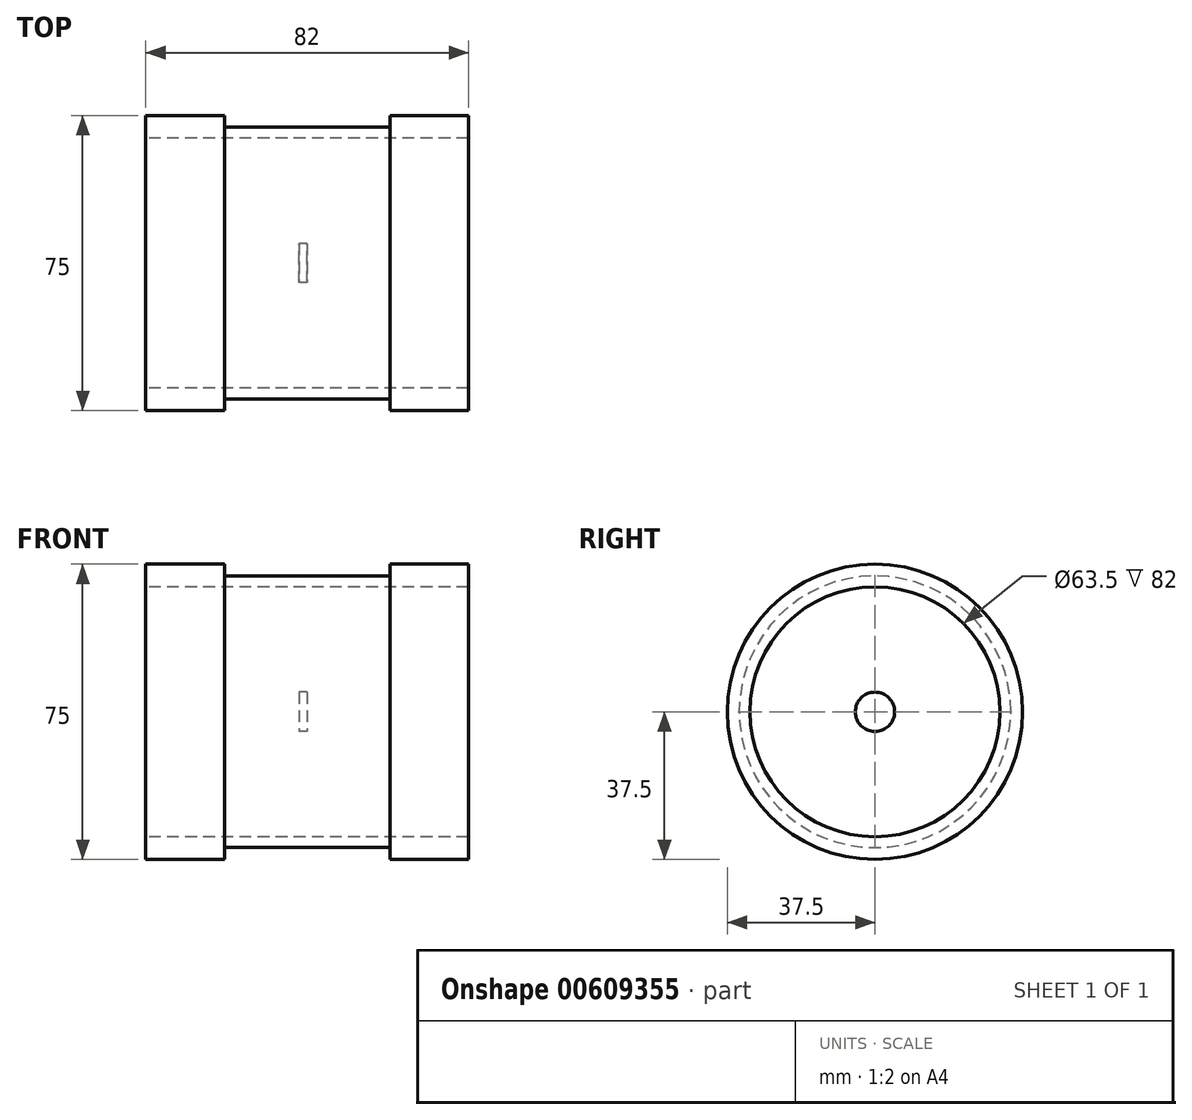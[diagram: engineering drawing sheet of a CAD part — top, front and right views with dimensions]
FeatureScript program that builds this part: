
annotation { "Feature Type Name" : "Feature", "Feature Type Description" : "" }
export const myFeature = defineFeature(function(context is Context, id is Id, definition is map)
    precondition{}
    {
        {
            var Q0;
            Q0=qCreatedBy(makeId("Front.planeOp"),FACE);
            var sketch = newSketch(context, id + "F0", { "sketchPlane" : qUnion([Q0])});
            skLineSegment(sketch, "E0", {"start": v(0, -31.75) * mm, "end": v(82, -31.75) * mm});
            skLineSegment(sketch, "E1", {"start": v(20, -34.5) * mm, "end": v(62, -34.5) * mm});
            skLineSegment(sketch, "E2", {"start": v(0, -37.5) * mm, "end": v(20, -37.5) * mm});
            skLineSegment(sketch, "E3", {"start": v(20, -37.5) * mm, "end": v(20, -34.5) * mm});
            skLineSegment(sketch, "E4", {"start": v(82, -31.75) * mm, "end": v(82, -37.5) * mm});
            skLineSegment(sketch, "E5", {"start": v(82, -37.5) * mm, "end": v(62, -37.5) * mm});
            skLineSegment(sketch, "E6", {"start": v(62, -37.5) * mm, "end": v(62, -34.5) * mm});
            skPoint(sketch, "E7.orphan", {"position": v(82, -34.5) * mm});
            skLineSegment(sketch, "E8", {"start": v(0, -31.75) * mm, "end": v(41, -31.75) * mm});
            skLineSegment(sketch, "E9", {"start": v(41, -31.75) * mm, "end": v(41, -34.75) * mm});
            skPoint(sketch, "E9.endSnap0", {"position": v(41, -34.5) * mm});
            skLineSegment(sketch, "E10", {"start": v(0, 0) * mm, "end": v(82, 0) * mm});
            skLineSegment(sketch, "E11", {"start": v(0, -31.75) * mm, "end": v(0, -37.5) * mm});
            skSolve(sketch);
        }
        {
            var Q0;
            Q0=qCreatedBy(makeId("Front.planeOp"),FACE);
            var sketch = newSketch(context, id + "F1", { "sketchPlane" : qUnion([Q0])});
            skLineSegment(sketch, "E12", {"start": v(39.93, 0) * mm, "end": v(38.93, 0) * mm});
            skLineSegment(sketch, "E13", {"start": v(38.93, 0) * mm, "end": v(38.93, -5) * mm});
            skLineSegment(sketch, "E14", {"start": v(38.93, -5) * mm, "end": v(40.93, -5) * mm});
            skLineSegment(sketch, "E15", {"start": v(40.93, -5) * mm, "end": v(40.93, 0) * mm});
            skLineSegment(sketch, "E16", {"start": v(40.93, 0) * mm, "end": v(39.93, 0) * mm});
            skSolve(sketch);
        }
        {
            var Q0;
            Q0=makeQuery(id+"F1.imprint","IMPRINT",FACE,{"disambiguationData":[TD([[makeQuery(id+"F1.imprint","IMPRINT",EDGE,{"derivedFrom":sQuery(id+"F1.wireOp",EDGE,"E12")}),1.0]])]});
            var Q1;
            Q1=makeQuery(id+"F0.imprint","IMPRINT",FACE,{"disambiguationData":[TD([[makeQuery(id+"F0.imprint","IMPRINT",EDGE,{"derivedFrom":sQuery(id+"F0.wireOp",EDGE,"E2")}),1.0]])]});
            var Q2;
            {var subQ4=sQuery(id+"F0.wireOp",EDGE,"E0");Q2=makeQuery(id+"F0.imprint","IMPRINT",FACE,{"disambiguationData":[TD([[makeQuery(id+"F0.imprint","IMPRINT",EDGE,{"derivedFrom":subQ4}),-1.0]])]});}
            var Q3;
            Q3=sQuery(id+"F0.wireOp",EDGE,"E10");
            revolve(context, id + "F2", {"entities" : qUnion([Q0, Q1, Q2]), "axis" : qUnion([Q3]), "revolveType" : RevolveType.FULL});
        }
    });
